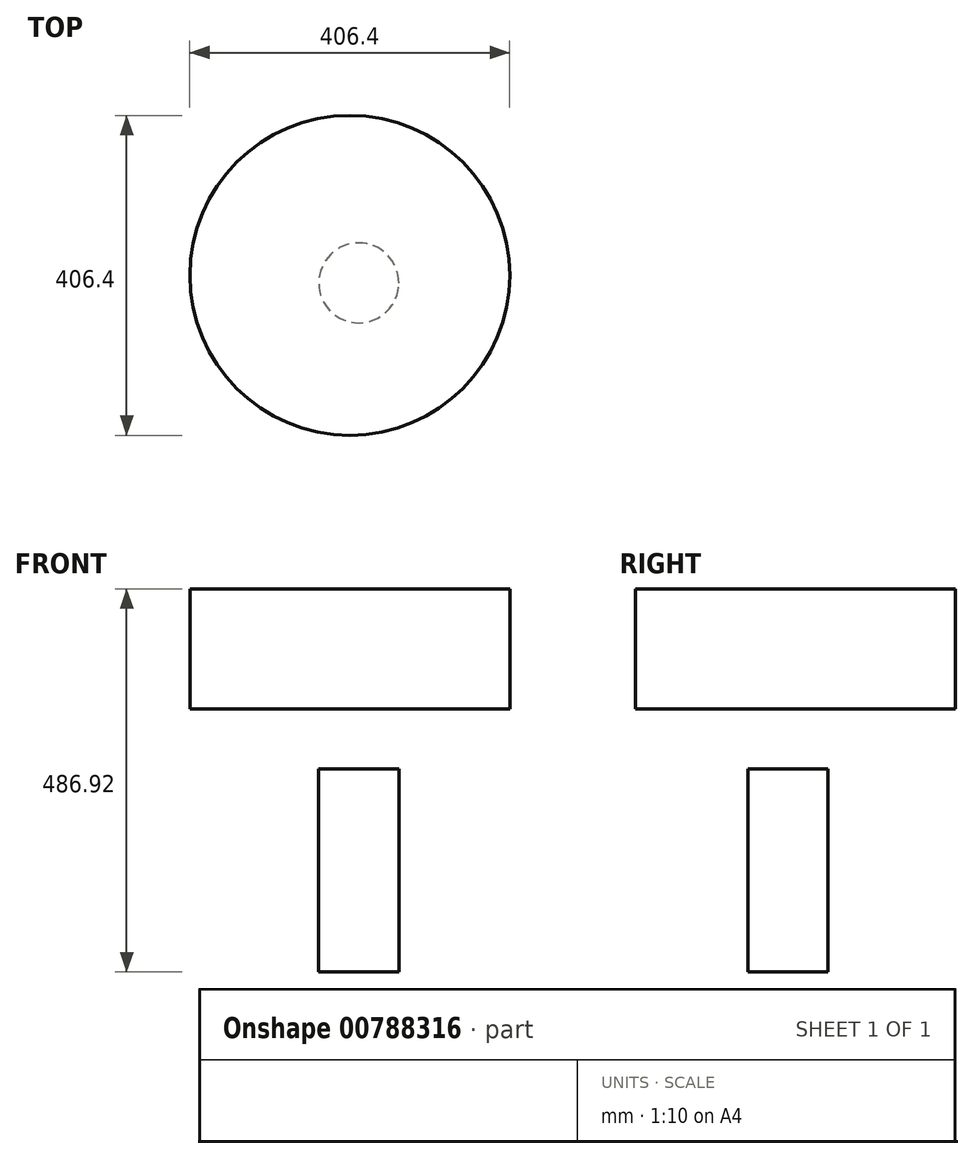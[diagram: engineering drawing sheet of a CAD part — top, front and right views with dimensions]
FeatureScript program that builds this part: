
annotation { "Feature Type Name" : "Feature", "Feature Type Description" : "" }
export const myFeature = defineFeature(function(context is Context, id is Id, definition is map)
    precondition{}
    {
        {
            var Q0;
            Q0=qCreatedBy(makeId("Top.planeOp"),FACE);
            var sketch = newSketch(context, id + "F0", { "sketchPlane" : qUnion([Q0])});
            skCircle(sketch, "E0", {"center": v(0, 0) * mm, "radius": 50.8 * mm});
            skSolve(sketch);
        }
        {
            var Q0;
            Q0 = qSketchRegion(id + "F0", true);
            extrude(context, id + "F1", {"entities" : qUnion([Q0]), "depth" : 258.32 * mm, "offsetDistance" : 25.4 * mm});
        }
        {
            var Q0;
            Q0=makeQuery(id+"F1.opExtrude","CAP_FACE",FACE,{"disambiguationData":[OSD([sQuery(id+"F0.wireOp",EDGE,"E0")])],"isStart":false});
            cPlane(context, id + "F2", {"entities" : qUnion([Q0]), "cplaneType" : CPlaneType.OFFSET, "offset" : 76.2 * mm, "width" : 152.4 * mm, "height" : 152.4 * mm});
        }
        {
            var Q0;
            Q0=qCreatedBy(id+"F2.planeOp",FACE);
            var sketch = newSketch(context, id + "F3", { "sketchPlane" : qUnion([Q0])});
            skCircle(sketch, "E1", {"center": v(-11.45, 9.64) * mm, "radius": 203.2 * mm});
            skSolve(sketch);
        }
        {
            var Q0;
            Q0 = qSketchRegion(id + "F3", true);
            extrude(context, id + "F4", {"entities" : qUnion([Q0]), "depth" : 152.4 * mm, "offsetDistance" : 25.4 * mm});
        }
    });
